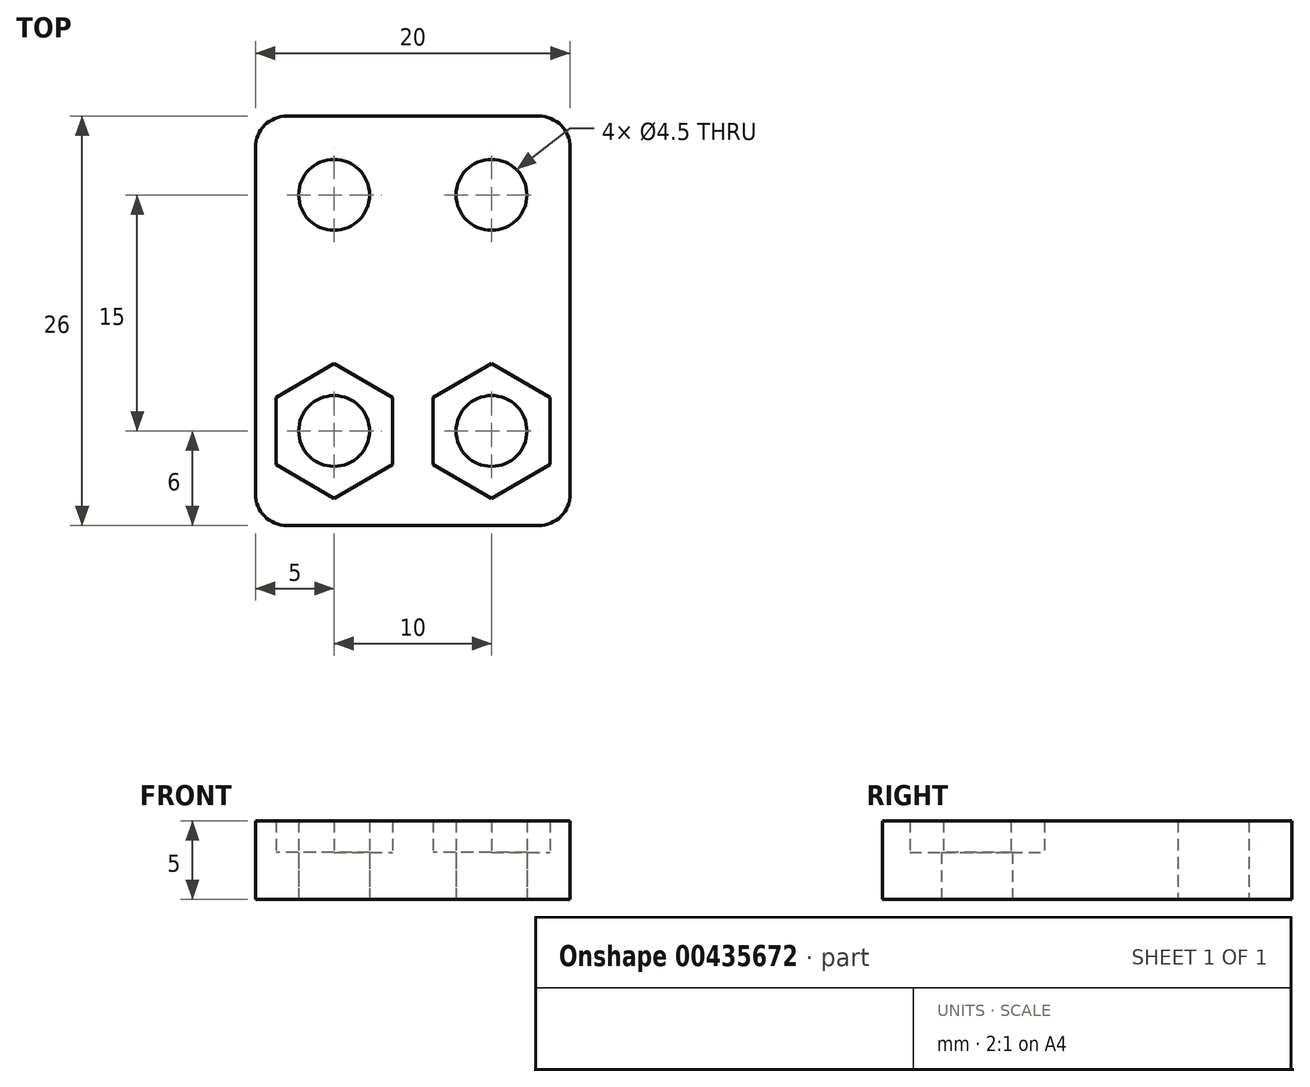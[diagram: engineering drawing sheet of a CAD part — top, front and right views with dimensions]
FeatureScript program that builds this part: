
annotation { "Feature Type Name" : "Feature", "Feature Type Description" : "" }
export const myFeature = defineFeature(function(context is Context, id is Id, definition is map)
    precondition{}
    {
        {
            var Q0;
            Q0=qCreatedBy(makeId("Top.planeOp"),FACE);
            var sketch = newSketch(context, id + "F0", { "sketchPlane" : qUnion([Q0])});
            skLineSegment(sketch, "E0.bottom", {"start": v(2, 0) * mm, "end": v(18, 0) * mm});
            skLineSegment(sketch, "E0.top", {"start": v(2, 26) * mm, "end": v(18, 26) * mm});
            skLineSegment(sketch, "E0.left", {"start": v(0, 2) * mm, "end": v(0, 24) * mm});
            skLineSegment(sketch, "E0.right", {"start": v(20, 2) * mm, "end": v(20, 24) * mm});
            skCircle(sketch, "E1", {"center": v(5, 21) * mm, "radius": 2.25 * mm});
            skCircle(sketch, "E2", {"center": v(15, 21) * mm, "radius": 2.25 * mm});
            skCircle(sketch, "E3", {"center": v(5, 6) * mm, "radius": 2.25 * mm});
            skCircle(sketch, "E4", {"center": v(15, 6) * mm, "radius": 2.25 * mm});
            skPoint(sketch, "E5.visualSharp", {"position": v(0, 26) * mm});
            skArc(sketch, "E5.filletArc", {"start": v(2, 26) * mm, "mid": v(0.59, 25.41) * mm, "end": v(0, 24) * mm});
            skPoint(sketch, "E6.visualSharp", {"position": v(20, 26) * mm});
            skArc(sketch, "E6.filletArc", {"start": v(20, 24) * mm, "mid": v(19.41, 25.41) * mm, "end": v(18, 26) * mm});
            skPoint(sketch, "E7.visualSharp", {"position": v(20, 0) * mm});
            skArc(sketch, "E7.filletArc", {"start": v(18, 0) * mm, "mid": v(19.41, 0.59) * mm, "end": v(20, 2) * mm});
            skPoint(sketch, "E8.visualSharp", {"position": v(0, 0) * mm});
            skArc(sketch, "E8.filletArc", {"start": v(0, 2) * mm, "mid": v(0.59, 0.59) * mm, "end": v(2, 0) * mm});
            skCircle(sketch, "E9.cCircle", {"center": v(5, 6) * mm, "radius": 3.7 * mm, "construction": true});
            skLineSegment(sketch, "E9.0", {"start": v(1.3, 3.86) * mm, "end": v(1.3, 8.14) * mm});
            skLineSegment(sketch, "E9.1", {"start": v(1.3, 8.14) * mm, "end": v(5, 10.27) * mm});
            skLineSegment(sketch, "E9.2", {"start": v(5, 10.27) * mm, "end": v(8.7, 8.14) * mm});
            skLineSegment(sketch, "E9.3", {"start": v(8.7, 8.14) * mm, "end": v(8.7, 3.86) * mm});
            skLineSegment(sketch, "E9.4", {"start": v(8.7, 3.86) * mm, "end": v(5, 1.73) * mm});
            skLineSegment(sketch, "E9.5", {"start": v(5, 1.73) * mm, "end": v(1.3, 3.86) * mm});
            skPoint(sketch, "E9.0.midPoint", {"position": v(1.3, 6) * mm});
            skCircle(sketch, "E10.cCircle", {"center": v(15, 6) * mm, "radius": 3.7 * mm, "construction": true});
            skLineSegment(sketch, "E10.0", {"start": v(11.3, 3.86) * mm, "end": v(11.3, 8.14) * mm});
            skLineSegment(sketch, "E10.1", {"start": v(11.3, 8.14) * mm, "end": v(15, 10.27) * mm});
            skLineSegment(sketch, "E10.2", {"start": v(15, 10.27) * mm, "end": v(18.7, 8.14) * mm});
            skLineSegment(sketch, "E10.3", {"start": v(18.7, 8.14) * mm, "end": v(18.7, 3.86) * mm});
            skLineSegment(sketch, "E10.4", {"start": v(18.7, 3.86) * mm, "end": v(15, 1.73) * mm});
            skLineSegment(sketch, "E10.5", {"start": v(15, 1.73) * mm, "end": v(11.3, 3.86) * mm});
            skPoint(sketch, "E10.0.midPoint", {"position": v(11.3, 6) * mm});
            skSolve(sketch);
        }
        {
            var Q0;
            Q0=makeQuery(id+"F0.imprint","IMPRINT",FACE,{"disambiguationData":[TD([[makeQuery(id+"F0.imprint","IMPRINT",EDGE,{"derivedFrom":sQuery(id+"F0.wireOp",EDGE,"E0.bottom")}),1.0]])]});
            extrude(context, id + "F1", {"entities" : qUnion([Q0]), "offsetDistance" : 25 * mm, "depth" : 5 * mm});
        }
        {
            var Q0;
            Q0=makeQuery(id+"F0.imprint","IMPRINT",FACE,{"disambiguationData":[TD([[makeQuery(id+"F0.imprint","IMPRINT",EDGE,{"derivedFrom":sQuery(id+"F0.wireOp",EDGE,"E3")}),-1.0]])]});
            var Q1;
            Q1=makeQuery(id+"F0.imprint","IMPRINT",FACE,{"disambiguationData":[TD([[makeQuery(id+"F0.imprint","IMPRINT",EDGE,{"derivedFrom":sQuery(id+"F0.wireOp",EDGE,"E4")}),-1.0]])]});
            extrude(context, id + "F2", {"entities" : qUnion([Q0, Q1]), "operationType" : NewBodyOperationType.ADD, "offsetDistance" : 25 * mm, "depth" : 3 * mm});
        }
    });
